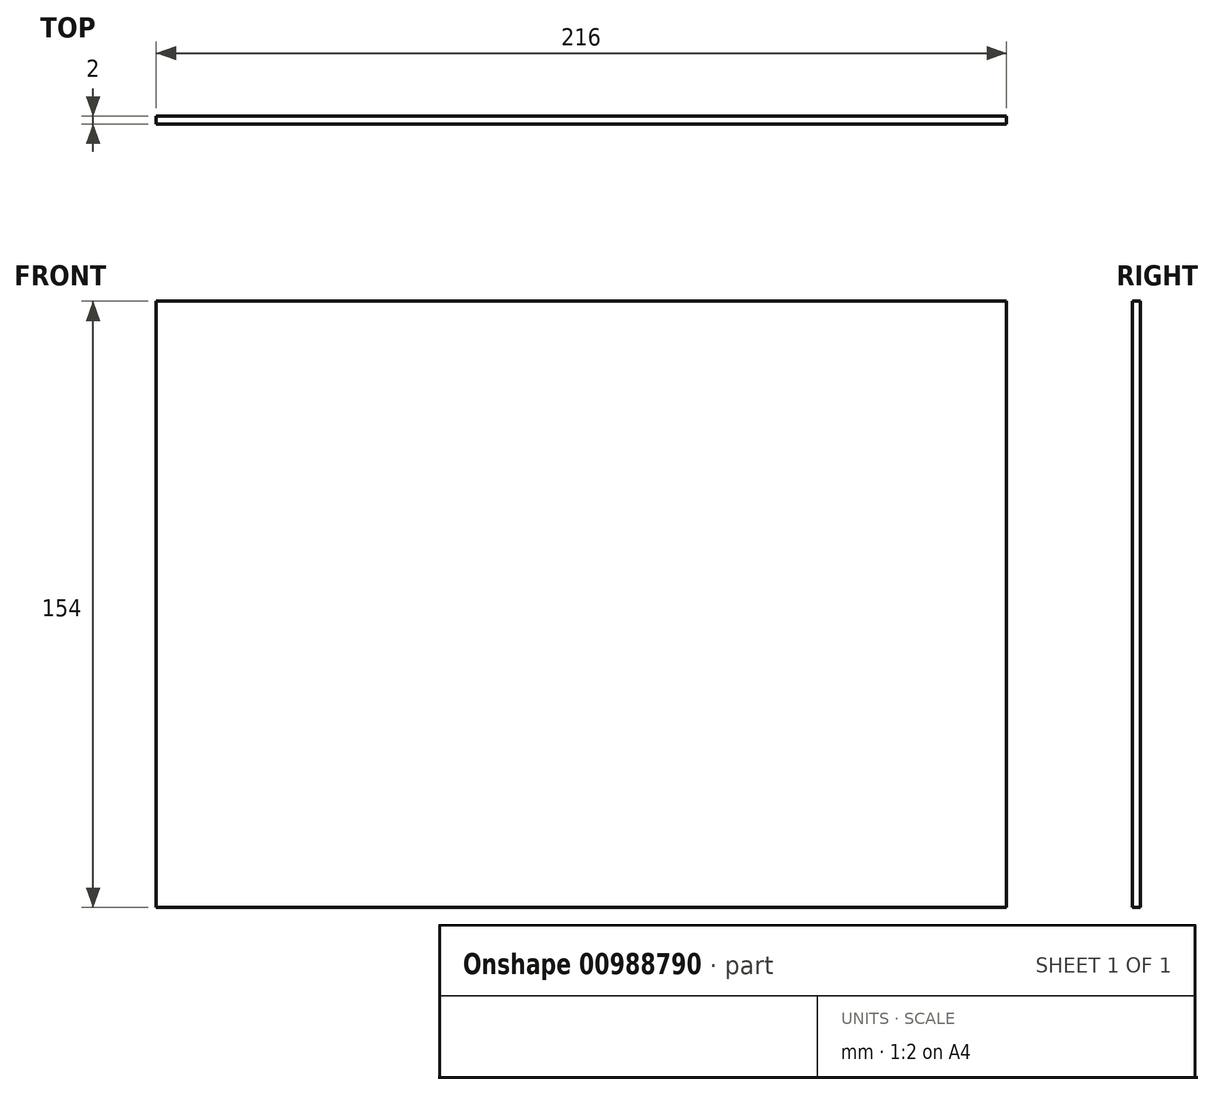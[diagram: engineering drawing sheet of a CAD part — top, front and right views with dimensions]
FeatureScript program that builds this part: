
annotation { "Feature Type Name" : "Feature", "Feature Type Description" : "" }
export const myFeature = defineFeature(function(context is Context, id is Id, definition is map)
    precondition{}
    {
        {
            var Q0;
            Q0=qCreatedBy(makeId("Front.planeOp"),FACE);
            var sketch = newSketch(context, id + "F0", { "sketchPlane" : qUnion([Q0])});
            skLineSegment(sketch, "E0.bottom", {"start": v(108, 77) * mm, "end": v(-108, 77) * mm});
            skLineSegment(sketch, "E0.top", {"start": v(108, -77) * mm, "end": v(-108, -77) * mm});
            skLineSegment(sketch, "E0.left", {"start": v(108, 77) * mm, "end": v(108, -77) * mm});
            skLineSegment(sketch, "E0.right", {"start": v(-108, 77) * mm, "end": v(-108, -77) * mm});
            skPoint(sketch, "E0.middle", {"position": v(0, 0) * mm});
            skSolve(sketch);
        }
        {
            var Q0;
            Q0=makeQuery(id+"F0.imprint","IMPRINT",FACE,{"disambiguationData":[TD([[makeQuery(id+"F0.imprint","IMPRINT",EDGE,{"derivedFrom":sQuery(id+"F0.wireOp",EDGE,"E0.bottom")}),1.0]])]});
            extrude(context, id + "F1", {"entities" : qUnion([Q0]), "depth" : 2 * mm, "offsetDistance" : 25 * mm});
        }
    });
